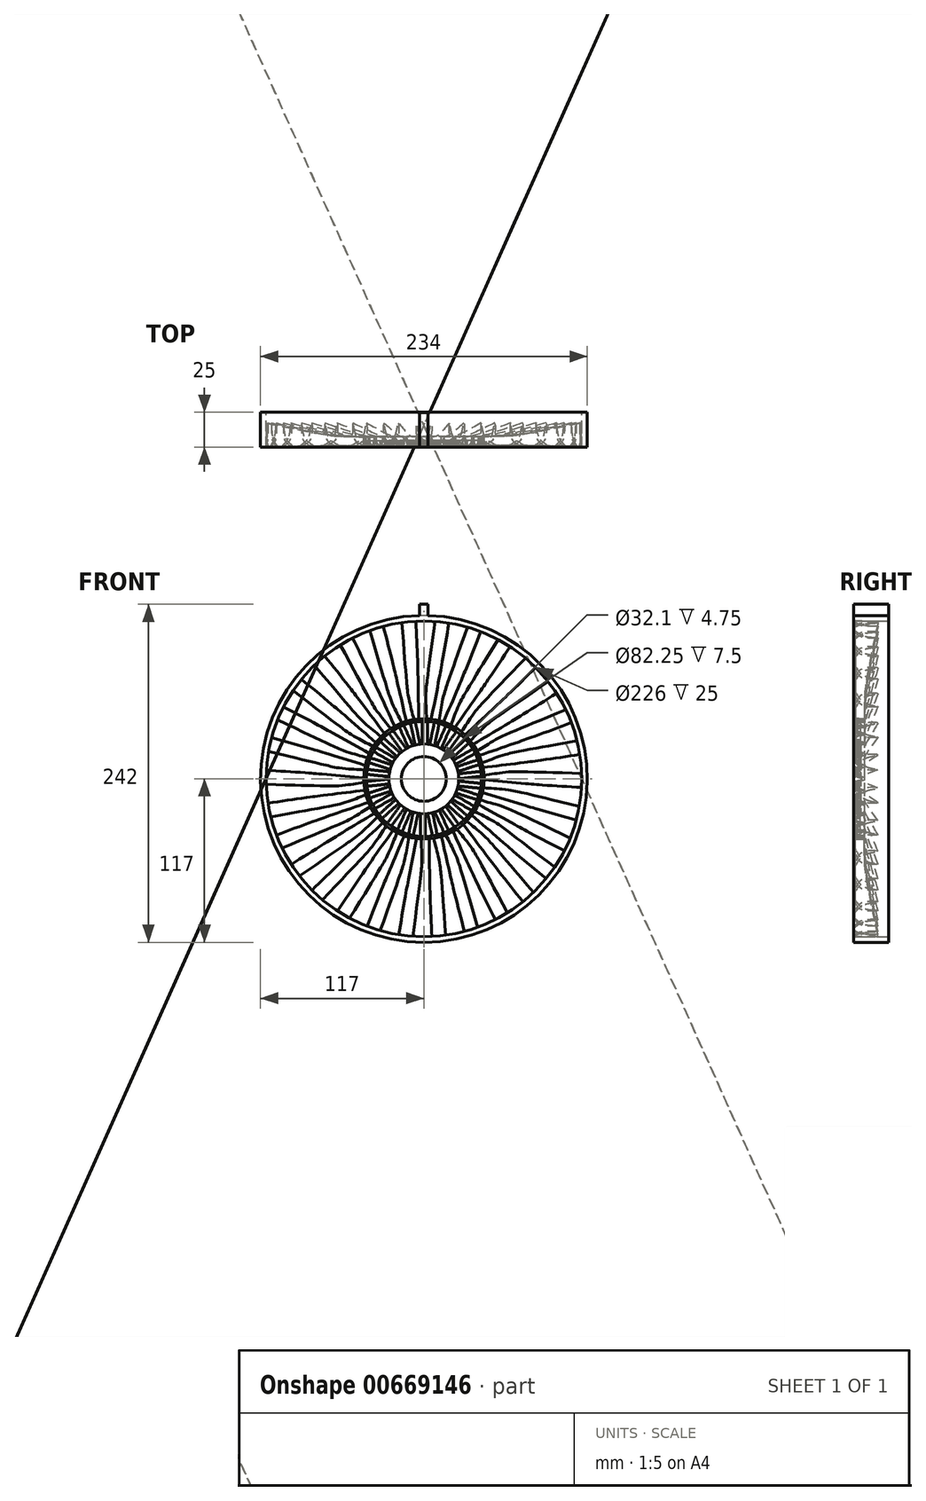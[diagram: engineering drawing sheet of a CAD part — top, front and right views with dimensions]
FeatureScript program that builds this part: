
annotation { "Feature Type Name" : "Feature", "Feature Type Description" : "" }
export const myFeature = defineFeature(function(context is Context, id is Id, definition is map)
    precondition{}
    {
        {
            var Q0;
            Q0=qCreatedBy(makeId("Right.planeOp"),FACE);
            var sketch = newSketch(context, id + "F0", { "sketchPlane" : qUnion([Q0])});
            skLineSegment(sketch, "E0", {"start": v(-12.34, 16.05) * mm, "end": v(-7.6, 16.05) * mm});
            skLineSegment(sketch, "E1", {"start": v(-7.6, 16.05) * mm, "end": v(-7.6, 25) * mm});
            skLineSegment(sketch, "E2", {"start": v(-7.6, 25) * mm, "end": v(-12.34, 25) * mm});
            skLineSegment(sketch, "E3", {"start": v(-12.34, 25) * mm, "end": v(-12.34, 16.05) * mm});
            skLineSegment(sketch, "E4", {"start": v(0, 0) * mm, "end": v(-25.16, 0) * mm, "construction": true});
            skSolve(sketch);
        }
        {
            var Q0;
            Q0 = qSketchRegion(id + "F0", true);
            var Q1;
            Q1=sQuery(id+"F0.wireOp",EDGE,"E4");
            revolve(context, id + "F1", {"entities" : qUnion([Q0]), "axis" : qUnion([Q1]), "revolveType" : RevolveType.FULL});
        }
        {
            var Q0;
            Q0=qCreatedBy(makeId("Top.planeOp"),FACE);
            cPlane(context, id + "F2", {"entities" : qUnion([Q0]), "cplaneType" : CPlaneType.OFFSET, "offset" : 24 * mm, "width" : 150 * mm, "height" : 150 * mm});
        }
        {
            var Q0;
            Q0=qCreatedBy(id+"F2.planeOp",FACE);
            var sketch = newSketch(context, id + "F3", { "sketchPlane" : qUnion([Q0])});
            skFitSpline(sketch, "E5", {"points": [v(-0.83, -7.67) * mm, v(-1.03, -9.3) * mm, v(0.56, -11.86) * mm, v(2.49, -12.3) * mm, v(1, -11.42) * mm, v(-0.52, -9.66) * mm, v(-0.83, -7.67) * mm]});
            skSolve(sketch);
        }
        {
            var Q0;
            Q0 = qSketchRegion(id + "F3", true);
            extrude(context, id + "F4", {"entities" : qUnion([Q0]), "operationType" : NewBodyOperationType.ADD, "depth" : (41.25 - 24) * mm, "offsetDistance" : 25 * mm});
        }
        {
            var Q0;
            Q0=makeQuery(id+"F4.opExtrude","SWEPT_FACE",FACE,{"disambiguationData":[OSD([sQuery(id+"F3.wireOp",EDGE,"E5")])]});
            var Q1;
            Q1=makeQuery(id+"F4.opExtrude","CAP_FACE",FACE,{"disambiguationData":[OSD([sQuery(id+"F3.wireOp",EDGE,"E5")])],"isStart":false});
            var Q2;
            Q2=makeQuery(id+"F1.opRevolve","SWEPT_EDGE",EDGE,{"disambiguationData":[OSD([sQuery(id+"F0.wireOp",EDGE,"E2"),sQuery(id+"F0.wireOp",EDGE,"E3")])]});
            circularPattern(context, id + "F5", {"patternType" : PatternType.FACE, "faces" : qUnion([Q0, Q1]), "axis" : qUnion([Q2]), "angle" : 360 * degree, "instanceCount" : 30, "equalSpace" : true});
        }
        {
            var Q0;
            Q0=qCreatedBy(makeId("Right.planeOp"),FACE);
            var sketch = newSketch(context, id + "F6", { "sketchPlane" : qUnion([Q0])});
            skLineSegment(sketch, "E6.bottom", {"start": v(-12.4, 41.12) * mm, "end": v(-4.9, 41.12) * mm});
            skLineSegment(sketch, "E6.top", {"start": v(-12.4, 43.13) * mm, "end": v(-4.9, 43.13) * mm});
            skLineSegment(sketch, "E6.left", {"start": v(-12.4, 41.12) * mm, "end": v(-12.4, 43.13) * mm});
            skLineSegment(sketch, "E6.right", {"start": v(-4.9, 41.12) * mm, "end": v(-4.9, 43.13) * mm});
            skLineSegment(sketch, "E7", {"start": v(0, 0) * mm, "end": v(-16.68, 0) * mm});
            skSolve(sketch);
        }
        {
            var Q0;
            Q0 = qSketchRegion(id + "F6", true);
            var Q1;
            Q1=sQuery(id+"F6.wireOp",EDGE,"E7");
            revolve(context, id + "F7", {"operationType" : NewBodyOperationType.ADD, "entities" : qUnion([Q0]), "axis" : qUnion([Q1]), "revolveType" : RevolveType.FULL});
        }
        {
            var Q0;
            Q0=qCreatedBy(id+"F2.planeOp",FACE);
            cPlane(context, id + "F8", {"entities" : qUnion([Q0]), "cplaneType" : CPlaneType.OFFSET, "offset" : 18 * mm, "width" : 150 * mm, "height" : 150 * mm});
        }
        {
            var Q0;
            Q0=qCreatedBy(makeId("Front.planeOp"),FACE);
            var sketch = newSketch(context, id + "F9", { "sketchPlane" : qUnion([Q0])});
            skCircle(sketch, "E8", {"center": v(0, 0) * mm, "radius": 114 * mm});
            skSolve(sketch);
        }
        {
            var Q0;
            Q0=qCreatedBy(id+"F8.planeOp",FACE);
            var sketch = newSketch(context, id + "F10", { "sketchPlane" : qUnion([Q0])});
            skFitSpline(sketch, "E9", {"points": [v(-3.63, -4.99) * mm, v(-2.77, -8.65) * mm, v(-0.6, -10.77) * mm, v(2.02, -12.1) * mm, v(-1.04, -11.63) * mm, v(-3.47, -9.15) * mm, v(-3.63, -4.99) * mm]});
            skSolve(sketch);
        }
        {
            var Q0;
            Q0=qCreatedBy(makeId("Top.planeOp"),FACE);
            cPlane(context, id + "F11", {"entities" : qUnion([Q0]), "cplaneType" : CPlaneType.OFFSET, "offset" : 114 * mm, "width" : 150 * mm, "height" : 150 * mm});
        }
        {
            var Q0;
            Q0=qCreatedBy(id+"F11.planeOp",FACE);
            var sketch = newSketch(context, id + "F12", { "sketchPlane" : qUnion([Q0])});
            skFitSpline(sketch, "E10", {"points": [v(-5.34, 5.16) * mm, v(-3.73, -1.75) * mm, v(1.56, -8.47) * mm, v(8.1, -11.97) * mm, v(0, -9.78) * mm, v(-5.4, -3.5) * mm, v(-5.34, 5.16) * mm]});
            skSolve(sketch);
        }
        {
            var Q1;
            Q1 = qSketchRegion(id + "F10", true);
            var Q2;
            Q2 = qSketchRegion(id + "F12", true);
            loft(context, id + "F13", {"operationType" : NewBodyOperationType.ADD, "sheetProfilesArray" : [{ "sheetProfileEntities" : qUnion([Q1]) }, { "sheetProfileEntities" : qUnion([Q2]) }]});
        }
        {
            var Q0;
            Q0=qCreatedBy(makeId("Right.planeOp"),FACE);
            var sketch = newSketch(context, id + "F14", { "sketchPlane" : qUnion([Q0])});
            skLineSegment(sketch, "E11.bottom", {"start": v(-12.4, 113) * mm, "end": v(12.6, 113) * mm});
            skLineSegment(sketch, "E11.top", {"start": v(-12.4, 117) * mm, "end": v(12.6, 117) * mm});
            skLineSegment(sketch, "E11.left", {"start": v(-12.4, 113) * mm, "end": v(-12.4, 117) * mm});
            skLineSegment(sketch, "E11.right", {"start": v(12.6, 113) * mm, "end": v(12.6, 117) * mm});
            skLineSegment(sketch, "E12", {"start": v(17.73, 0) * mm, "end": v(-27.1, 0) * mm, "construction": true});
            skSolve(sketch);
        }
        {
            var Q0;
            Q0 = qSketchRegion(id + "F14", true);
            var Q1;
            Q1=sQuery(id+"F14.wireOp",EDGE,"E12");
            revolve(context, id + "F15", {"operationType" : NewBodyOperationType.ADD, "entities" : qUnion([Q0]), "axis" : qUnion([Q1]), "revolveType" : RevolveType.FULL});
        }
        {
            var Q0;
            Q0=makeQuery(id+"F13.opLoft","SWEPT_FACE",FACE,{"disambiguationData":[OSD([sQuery(id+"F10.wireOp",EDGE,"E9"),sQuery(id+"F12.wireOp",EDGE,"E10")])]});
            var Q1;
            Q1=makeQuery(id+"F13.opLoft","CAP_FACE",FACE,{"disambiguationData":[OSD([makeQuery(id+"F12.imprint","IMPRINT",FACE,{"disambiguationData":[TD([[makeQuery(id+"F12.imprint","IMPRINT",EDGE,{"derivedFrom":sQuery(id+"F12.wireOp",EDGE,"E10")}),-1.0]])]})])],"isStart":true});
            var Q2;
            Q2=makeQuery(id+"F7.opRevolve","SWEPT_EDGE",EDGE,{"disambiguationData":[OSD([sQuery(id+"F6.wireOp",EDGE,"E6.top"),sQuery(id+"F6.wireOp",EDGE,"E6.left")])]});
            circularPattern(context, id + "F16", {"patternType" : PatternType.FACE, "faces" : qUnion([Q0, Q1]), "axis" : qUnion([Q2]), "angle" : 360 * degree, "instanceCount" : 30, "equalSpace" : true});
        }
        {
            var Q0;
            Q0=qCreatedBy(makeId("Top.planeOp"),FACE);
            cPlane(context, id + "F17", {"entities" : qUnion([Q0]), "cplaneType" : CPlaneType.OFFSET, "offset" : 115 * mm, "width" : 150 * mm, "height" : 150 * mm});
        }
        {
            var Q0;
            Q0=qCreatedBy(id+"F17.planeOp",FACE);
            var sketch = newSketch(context, id + "F18", { "sketchPlane" : qUnion([Q0])});
            skLineSegment(sketch, "E13.bottom", {"start": v(3, 12.4) * mm, "end": v(-3, 12.4) * mm});
            skLineSegment(sketch, "E13.top", {"start": v(3, -12.4) * mm, "end": v(-3, -12.4) * mm});
            skLineSegment(sketch, "E13.left", {"start": v(3, 12.4) * mm, "end": v(3, -12.4) * mm});
            skLineSegment(sketch, "E13.right", {"start": v(-3, 12.4) * mm, "end": v(-3, -12.4) * mm});
            skPoint(sketch, "E13.middle", {"position": v(0, 0) * mm});
            skSolve(sketch);
        }
        {
            var Q0;
            Q0 = qSketchRegion(id + "F18", true);
            extrude(context, id + "F19", {"entities" : qUnion([Q0]), "operationType" : NewBodyOperationType.ADD, "depth" : 10 * mm, "offsetDistance" : 25 * mm});
        }
    });
